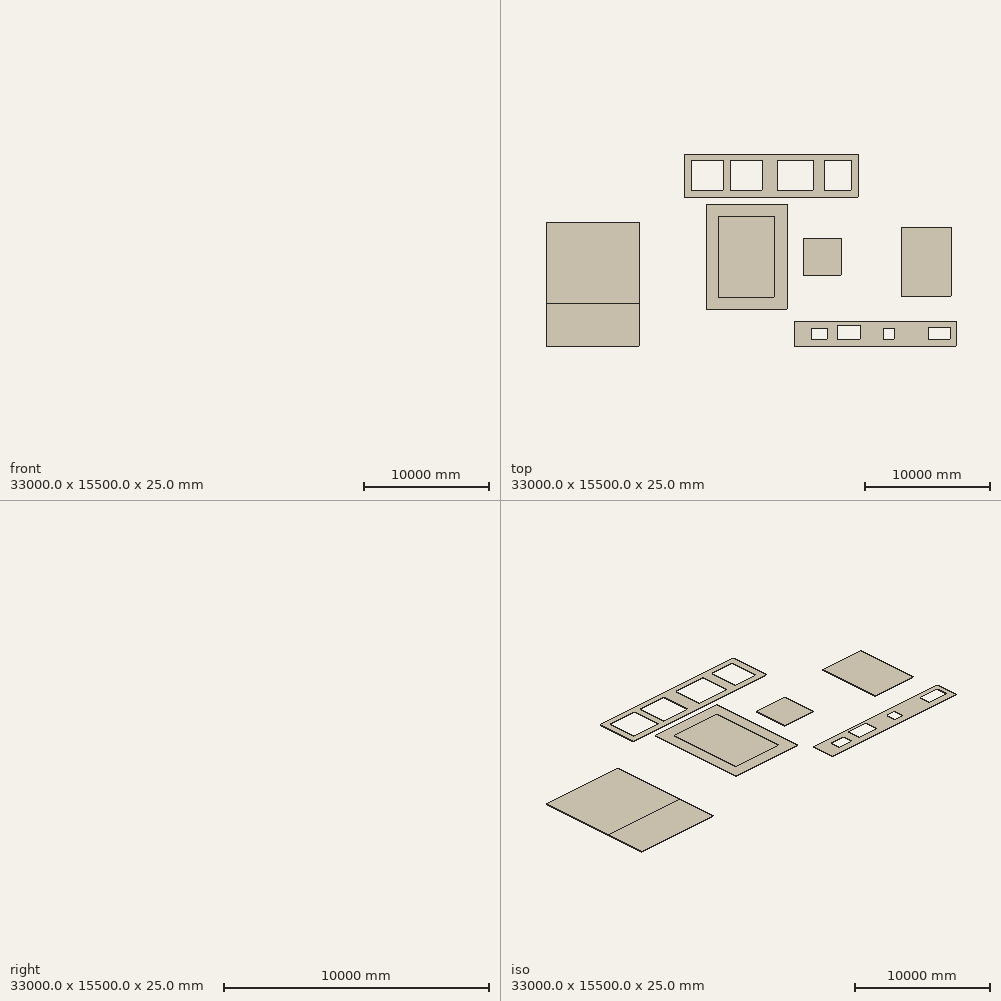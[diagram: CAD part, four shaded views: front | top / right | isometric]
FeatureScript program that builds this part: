
annotation { "Feature Type Name" : "Feature", "Feature Type Description" : "" }
export const myFeature = defineFeature(function(context is Context, id is Id, definition is map)
    precondition{}
    {
        {
            var Q0;
            Q0=qCreatedBy(makeId("Top.planeOp"),FACE);
            var sketch = newSketch(context, id + "F0", { "sketchPlane" : qUnion([Q0])});
            skLineSegment(sketch, "E0.bottom", {"start": v(0, 0) * mm, "end": v(33000, 0) * mm});
            skLineSegment(sketch, "E0.top", {"start": v(0, 23000) * mm, "end": v(33000, 23000) * mm});
            skLineSegment(sketch, "E0.left", {"start": v(0, 0) * mm, "end": v(0, 23000) * mm});
            skLineSegment(sketch, "E0.right", {"start": v(33000, 0) * mm, "end": v(33000, 23000) * mm});
            skLineSegment(sketch, "E1.bottom", {"start": v(5500, 0) * mm, "end": v(17500, 0) * mm});
            skLineSegment(sketch, "E1.top", {"start": v(5500, 7500) * mm, "end": v(17500, 7500) * mm});
            skLineSegment(sketch, "E1.left", {"start": v(5500, 0) * mm, "end": v(5500, 7500) * mm});
            skLineSegment(sketch, "E1.right", {"start": v(17500, 0) * mm, "end": v(17500, 7500) * mm});
            skLineSegment(sketch, "E2.bottom", {"start": v(33000, 0) * mm, "end": v(17500, 0) * mm});
            skLineSegment(sketch, "E2.top", {"start": v(33000, 7500) * mm, "end": v(17500, 7500) * mm});
            skLineSegment(sketch, "E2.left", {"start": v(33000, 0) * mm, "end": v(33000, 7500) * mm});
            skLineSegment(sketch, "E3.bottom", {"start": v(0, 11000) * mm, "end": v(7500, 11000) * mm});
            skLineSegment(sketch, "E3.top", {"start": v(0, 17500) * mm, "end": v(7500, 17500) * mm});
            skLineSegment(sketch, "E3.left", {"start": v(0, 11000) * mm, "end": v(0, 17500) * mm});
            skLineSegment(sketch, "E3.right", {"start": v(7500, 11000) * mm, "end": v(7500, 17500) * mm});
            skLineSegment(sketch, "E4.bottom", {"start": v(13874.13, 11466.42) * mm, "end": v(18374.13, 11466.42) * mm});
            skLineSegment(sketch, "E4.top", {"start": v(13874.13, 17966.42) * mm, "end": v(18374.13, 17966.42) * mm});
            skLineSegment(sketch, "E4.left", {"start": v(13874.13, 11466.42) * mm, "end": v(13874.13, 17966.42) * mm});
            skLineSegment(sketch, "E4.right", {"start": v(18374.13, 11466.42) * mm, "end": v(18374.13, 17966.42) * mm});
            skLineSegment(sketch, "E5.bottom", {"start": v(20719.3, 16201.58) * mm, "end": v(23719.3, 16201.58) * mm});
            skLineSegment(sketch, "E5.top", {"start": v(20719.3, 13201.58) * mm, "end": v(23719.3, 13201.58) * mm});
            skLineSegment(sketch, "E5.left", {"start": v(20719.3, 16201.58) * mm, "end": v(20719.3, 13201.58) * mm});
            skLineSegment(sketch, "E5.right", {"start": v(23719.3, 16201.58) * mm, "end": v(23719.3, 13201.58) * mm});
            skLineSegment(sketch, "E6.bottom", {"start": v(32567.28, 17071.27) * mm, "end": v(28567.28, 17071.27) * mm});
            skLineSegment(sketch, "E6.top", {"start": v(32567.28, 11571.27) * mm, "end": v(28567.28, 11571.27) * mm});
            skLineSegment(sketch, "E6.left", {"start": v(32567.28, 17071.27) * mm, "end": v(32567.28, 11571.27) * mm});
            skLineSegment(sketch, "E6.right", {"start": v(28567.28, 17071.27) * mm, "end": v(28567.28, 11571.27) * mm});
            skLineSegment(sketch, "E7.bottom", {"start": v(32553.53, 8100.18) * mm, "end": v(30753.53, 8100.18) * mm});
            skLineSegment(sketch, "E7.top", {"start": v(32553.53, 9086.74) * mm, "end": v(30753.53, 9086.74) * mm});
            skLineSegment(sketch, "E7.left", {"start": v(32553.53, 8100.18) * mm, "end": v(32553.53, 9086.74) * mm});
            skLineSegment(sketch, "E7.right", {"start": v(30753.53, 8100.18) * mm, "end": v(30753.53, 9086.74) * mm});
            skLineSegment(sketch, "E8.bottom", {"start": v(27986.08, 8100.18) * mm, "end": v(27099.53, 8100.18) * mm});
            skLineSegment(sketch, "E8.top", {"start": v(27986.08, 8986.74) * mm, "end": v(27099.53, 8986.74) * mm});
            skLineSegment(sketch, "E8.left", {"start": v(27986.08, 8100.18) * mm, "end": v(27986.08, 8986.74) * mm});
            skLineSegment(sketch, "E8.right", {"start": v(27099.53, 8100.18) * mm, "end": v(27099.53, 8986.74) * mm});
            skLineSegment(sketch, "E9.bottom", {"start": v(25259.98, 8100.18) * mm, "end": v(23418.54, 8100.18) * mm});
            skLineSegment(sketch, "E9.top", {"start": v(25259.98, 9242.16) * mm, "end": v(23418.54, 9242.16) * mm});
            skLineSegment(sketch, "E9.left", {"start": v(25259.98, 8100.18) * mm, "end": v(25259.98, 9242.16) * mm});
            skLineSegment(sketch, "E9.right", {"start": v(23418.54, 8100.18) * mm, "end": v(23418.54, 9242.16) * mm});
            skLineSegment(sketch, "E10.bottom", {"start": v(22624.19, 8100.18) * mm, "end": v(21316.92, 8100.18) * mm});
            skLineSegment(sketch, "E10.top", {"start": v(22624.19, 8953.3) * mm, "end": v(21316.92, 8953.3) * mm});
            skLineSegment(sketch, "E10.left", {"start": v(22624.19, 8100.18) * mm, "end": v(22624.19, 8953.3) * mm});
            skLineSegment(sketch, "E10.right", {"start": v(21316.92, 8100.18) * mm, "end": v(21316.92, 8953.3) * mm});
            skLineSegment(sketch, "E11.bottom", {"start": v(11686.59, 22531.44) * mm, "end": v(14284.47, 22531.44) * mm});
            skLineSegment(sketch, "E11.top", {"start": v(11686.59, 20040.27) * mm, "end": v(14284.47, 20040.27) * mm});
            skLineSegment(sketch, "E11.left", {"start": v(11686.59, 22531.44) * mm, "end": v(11686.59, 20040.27) * mm});
            skLineSegment(sketch, "E11.right", {"start": v(14284.47, 22531.44) * mm, "end": v(14284.47, 20040.27) * mm});
            skLineSegment(sketch, "E12.bottom", {"start": v(14838.96, 22531.44) * mm, "end": v(17353.71, 22531.44) * mm});
            skLineSegment(sketch, "E12.top", {"start": v(14838.96, 20040.27) * mm, "end": v(17353.71, 20040.27) * mm});
            skLineSegment(sketch, "E12.left", {"start": v(14838.96, 22531.44) * mm, "end": v(14838.96, 20040.27) * mm});
            skLineSegment(sketch, "E12.right", {"start": v(17353.71, 22531.44) * mm, "end": v(17353.71, 20040.27) * mm});
            skLineSegment(sketch, "E13.bottom", {"start": v(18563.08, 22531.44) * mm, "end": v(21467.98, 22531.44) * mm});
            skLineSegment(sketch, "E13.top", {"start": v(18563.08, 20052.37) * mm, "end": v(21467.98, 20052.37) * mm});
            skLineSegment(sketch, "E13.left", {"start": v(18563.08, 22531.44) * mm, "end": v(18563.08, 20052.37) * mm});
            skLineSegment(sketch, "E13.right", {"start": v(21467.98, 22531.44) * mm, "end": v(21467.98, 20052.37) * mm});
            skLineSegment(sketch, "E14.bottom", {"start": v(22371.62, 22531.44) * mm, "end": v(24521.94, 22531.44) * mm});
            skLineSegment(sketch, "E14.top", {"start": v(22371.62, 20041.58) * mm, "end": v(24521.94, 20041.58) * mm});
            skLineSegment(sketch, "E14.left", {"start": v(22371.62, 22531.44) * mm, "end": v(22371.62, 20041.58) * mm});
            skLineSegment(sketch, "E14.right", {"start": v(24521.94, 22531.44) * mm, "end": v(24521.94, 20041.58) * mm});
            skLineSegment(sketch, "E15.bottom", {"start": v(11112.92, 23000) * mm, "end": v(25112.92, 23000) * mm});
            skLineSegment(sketch, "E15.top", {"start": v(11112.92, 19500) * mm, "end": v(25112.92, 19500) * mm});
            skLineSegment(sketch, "E15.left", {"start": v(11112.92, 23000) * mm, "end": v(11112.92, 19500) * mm});
            skLineSegment(sketch, "E15.right", {"start": v(25112.92, 23000) * mm, "end": v(25112.92, 19500) * mm});
            skLineSegment(sketch, "E16", {"start": v(6000, 17500) * mm, "end": v(6000, 23000) * mm});
            skLineSegment(sketch, "E17.bottom", {"start": v(20000, 9500) * mm, "end": v(33000, 9500) * mm});
            skLineSegment(sketch, "E17.top", {"start": v(20000, 7500) * mm, "end": v(33000, 7500) * mm});
            skLineSegment(sketch, "E17.left", {"start": v(20000, 9500) * mm, "end": v(20000, 7500) * mm});
            skLineSegment(sketch, "E17.right", {"start": v(33000, 9500) * mm, "end": v(33000, 7500) * mm});
            skLineSegment(sketch, "E18.bottom", {"start": v(6000, 17500) * mm, "end": v(8000, 17500) * mm});
            skLineSegment(sketch, "E18.top", {"start": v(6000, 23000) * mm, "end": v(8000, 23000) * mm});
            skLineSegment(sketch, "E18.right", {"start": v(8000, 17500) * mm, "end": v(8000, 23000) * mm});
            skLineSegment(sketch, "E19", {"start": v(5500, 7500) * mm, "end": v(5500, 11000) * mm});
            skLineSegment(sketch, "E20.top", {"start": v(0, 7500) * mm, "end": v(7500, 7500) * mm});
            skLineSegment(sketch, "E20.left", {"start": v(0, 11000) * mm, "end": v(0, 7500) * mm});
            skLineSegment(sketch, "E20.right", {"start": v(7500, 11000) * mm, "end": v(7500, 7500) * mm});
            skLineSegment(sketch, "E21.0", {"start": v(12874.13, 18966.42) * mm, "end": v(19374.13, 18966.42) * mm});
            skLineSegment(sketch, "E21.1", {"start": v(12874.13, 10466.42) * mm, "end": v(12874.13, 18966.42) * mm});
            skLineSegment(sketch, "E21.2", {"start": v(12874.13, 10466.42) * mm, "end": v(19374.13, 10466.42) * mm});
            skLineSegment(sketch, "E21.3", {"start": v(19374.13, 10466.42) * mm, "end": v(19374.13, 18966.42) * mm});
            skSolve(sketch);
        }
        {
            var Q0;
            Q0=makeQuery(id+"F0.imprint","IMPRINT",FACE,{"disambiguationData":[TD([[makeQuery(id+"F0.imprint","IMPRINT",EDGE,{"derivedFrom":sQuery(id+"F0.wireOp",EDGE,"E1.bottom")}),1.0]])]});
            var Q1;
            Q1=makeQuery(id+"F0.imprint","IMPRINT",FACE,{"disambiguationData":[TD([[makeQuery(id+"F0.imprint","IMPRINT",EDGE,{"derivedFrom":sQuery(id+"F0.wireOp",EDGE,"E6.bottom")}),1.0]])]});
            var Q2;
            Q2=makeQuery(id+"F0.imprint","IMPRINT",FACE,{"disambiguationData":[TD([[makeQuery(id+"F0.imprint","IMPRINT",EDGE,{"derivedFrom":sQuery(id+"F0.wireOp",EDGE,"E7.bottom")}),1.0]])]});
            var Q3;
            Q3=makeQuery(id+"F0.imprint","IMPRINT",FACE,{"disambiguationData":[TD([[makeQuery(id+"F0.imprint","IMPRINT",EDGE,{"derivedFrom":sQuery(id+"F0.wireOp",EDGE,"E11.bottom")}),1.0]])]});
            extrude(context, id + "F1", {"entities" : qUnion([Q0, Q1, Q2, Q3]), "depth" : 25 * mm, "offsetDistance" : 25 * mm});
        }
        {
            var Q0;
            Q0=makeQuery(id+"F0.imprint","IMPRINT",FACE,{"disambiguationData":[TD([[makeQuery(id+"F0.imprint","IMPRINT",EDGE,{"derivedFrom":sQuery(id+"F0.wireOp",EDGE,"E2.bottom")}),-1.0]])]});
            var Q1;
            Q1=makeQuery(id+"F0.imprint","IMPRINT",FACE,{"disambiguationData":[TD([[makeQuery(id+"F0.imprint","IMPRINT",EDGE,{"derivedFrom":sQuery(id+"F0.wireOp",EDGE,"E5.bottom")}),-1.0]])]});
            var Q2;
            Q2=makeQuery(id+"F0.imprint","IMPRINT",FACE,{"disambiguationData":[TD([[makeQuery(id+"F0.imprint","IMPRINT",EDGE,{"derivedFrom":sQuery(id+"F0.wireOp",EDGE,"E18.top")}),-1.0]])]});
            extrude(context, id + "F2", {"entities" : qUnion([Q0, Q1, Q2]), "depth" : 25 * mm, "offsetDistance" : 25 * mm});
        }
        {
            var Q0;
            Q0=makeQuery(id+"F0.imprint","IMPRINT",FACE,{"disambiguationData":[TD([[makeQuery(id+"F0.imprint","IMPRINT",EDGE,{"derivedFrom":sQuery(id+"F0.wireOp",EDGE,"E4.bottom")}),1.0]])]});
            extrude(context, id + "F3", {"entities" : qUnion([Q0]), "depth" : 25 * mm, "offsetDistance" : 25 * mm});
        }
        {
            var Q0;
            {var subQ1=sQuery(id+"F0.wireOp",EDGE,"E3.top");Q0=makeQuery(id+"F0.imprint","IMPRINT",FACE,{"disambiguationData":[TD([[makeQuery(id+"F0.imprint","IMPRINT",EDGE,{"derivedFrom":subQ1}),-1.0]])]});}
            extrude(context, id + "F4", {"entities" : qUnion([Q0]), "depth" : 25 * mm, "offsetDistance" : 25 * mm});
        }
        {
            var Q0;
            {var subQ0=sQuery(id+"F0.wireOp",EDGE,"E19");Q0=makeQuery(id+"F0.imprint","IMPRINT",FACE,{"disambiguationData":[TD([[makeQuery(id+"F0.imprint","IMPRINT",EDGE,{"derivedFrom":subQ0}),1.0]])]});}
            var Q1;
            {var subQ3=sQuery(id+"F0.wireOp",EDGE,"E19");Q1=makeQuery(id+"F0.imprint","IMPRINT",FACE,{"disambiguationData":[TD([[makeQuery(id+"F0.imprint","IMPRINT",EDGE,{"derivedFrom":subQ3}),-1.0]])]});}
            var Q2;
            Q2=makeQuery(id+"F0.imprint","IMPRINT",FACE,{"disambiguationData":[TD([[makeQuery(id+"F0.imprint","IMPRINT",EDGE,{"derivedFrom":sQuery(id+"F0.wireOp",EDGE,"E4.bottom")}),-1.0]])]});
            extrude(context, id + "F5", {"entities" : qUnion([Q0, Q1, Q2]), "depth" : 25 * mm, "offsetDistance" : 25 * mm});
        }
    });
